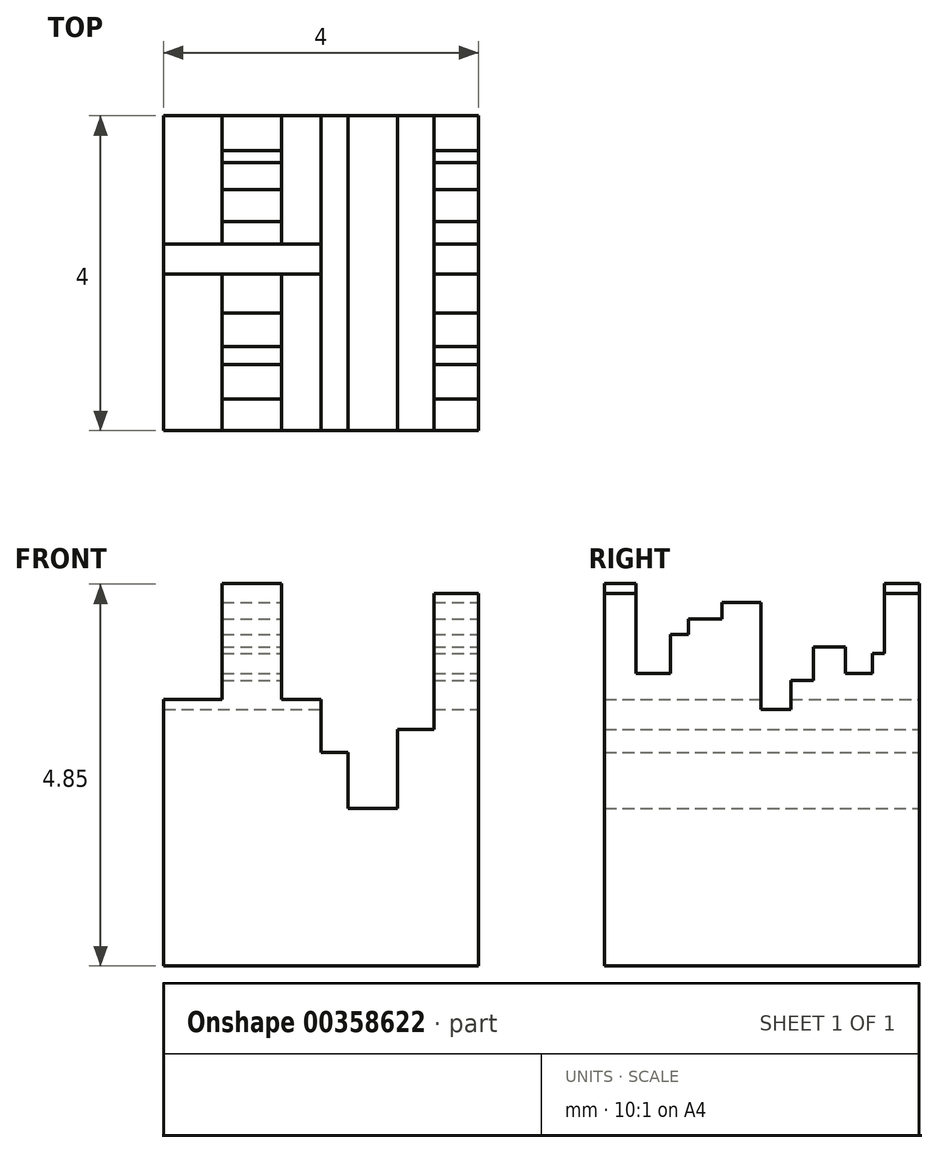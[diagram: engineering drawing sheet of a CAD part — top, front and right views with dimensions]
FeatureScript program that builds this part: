
annotation { "Feature Type Name" : "Feature", "Feature Type Description" : "" }
export const myFeature = defineFeature(function(context is Context, id is Id, definition is map)
    precondition{}
    {
        {
            var Q0;
            Q0=qCreatedBy(makeId("Front.planeOp"),FACE);
            var sketch = newSketch(context, id + "F0", { "sketchPlane" : qUnion([Q0])});
            skLineSegment(sketch, "E0.top", {"start": v(-2, -2) * mm, "end": v(2, -2) * mm});
            skLineSegment(sketch, "E0.left", {"start": v(-2, 1.38) * mm, "end": v(-2, -2) * mm});
            skLineSegment(sketch, "E0.right", {"start": v(2, 2) * mm, "end": v(2, -2) * mm});
            skPoint(sketch, "E0.middle", {"position": v(0, 0) * mm});
            skLineSegment(sketch, "E1", {"start": v(0.97, 1) * mm, "end": v(0.97, 0) * mm});
            skLineSegment(sketch, "E2", {"start": v(0.97, 0) * mm, "end": v(0.34, 0) * mm});
            skLineSegment(sketch, "E3", {"start": v(0.34, 0) * mm, "end": v(0.34, 0.71) * mm});
            skLineSegment(sketch, "E4", {"start": v(0.34, 0.71) * mm, "end": v(0, 0.71) * mm});
            skLineSegment(sketch, "E5", {"start": v(0, 0.71) * mm, "end": v(0, 1.38) * mm});
            skLineSegment(sketch, "E6", {"start": v(0, 1.38) * mm, "end": v(-0.5, 1.38) * mm});
            skLineSegment(sketch, "E7", {"start": v(-0.5, 1.38) * mm, "end": v(-0.5, 2) * mm});
            skLineSegment(sketch, "E8", {"start": v(-0.5, 2) * mm, "end": v(-0.5, 2.85) * mm});
            skLineSegment(sketch, "E9", {"start": v(-0.5, 2.85) * mm, "end": v(-1.26, 2.85) * mm});
            skLineSegment(sketch, "E10", {"start": v(-1.26, 2.85) * mm, "end": v(-1.26, 2) * mm});
            skLineSegment(sketch, "E11", {"start": v(-1.26, 2) * mm, "end": v(-1.26, 1.38) * mm});
            skLineSegment(sketch, "E12", {"start": v(-1.26, 1.38) * mm, "end": v(-2, 1.38) * mm});
            skLineSegment(sketch, "E13", {"start": v(0.97, 1) * mm, "end": v(1.43, 1) * mm});
            skLineSegment(sketch, "E14", {"start": v(1.43, 1) * mm, "end": v(1.43, 2.73) * mm});
            skLineSegment(sketch, "E15", {"start": v(1.43, 2.73) * mm, "end": v(1.94, 2.73) * mm});
            skPoint(sketch, "E16.start.orphan", {"position": v(0.97, 2) * mm});
            skPoint(sketch, "E17.orphan", {"position": v(-2, 2) * mm});
            skLineSegment(sketch, "E18", {"start": v(2, 2) * mm, "end": v(2, 2.73) * mm});
            skLineSegment(sketch, "E19", {"start": v(2, 2.73) * mm, "end": v(1.94, 2.73) * mm});
            skSolve(sketch);
        }
        {
            var Q0;
            Q0 = qSketchRegion(id + "F0", true);
            extrude(context, id + "F1", {"entities" : qUnion([Q0]), "depth" : 4 * mm});
        }
        {
            var Q0;
            Q0=makeQuery(id+"F1.opExtrude","SWEPT_FACE",FACE,{"disambiguationData":[OSD([sQuery(id+"F0.wireOp",EDGE,"E0.right"),sQuery(id+"F0.wireOp",EDGE,"E18")])]});
            var sketch = newSketch(context, id + "F2", { "sketchPlane" : qUnion([Q0])});
            skLineSegment(sketch, "E20", {"start": v(-3.6, 2.73) * mm, "end": v(-3.6, 1.71) * mm});
            skLineSegment(sketch, "E21", {"start": v(-3.6, 1.71) * mm, "end": v(-3.16, 1.71) * mm});
            skLineSegment(sketch, "E22", {"start": v(-3.16, 1.71) * mm, "end": v(-3.16, 2.21) * mm});
            skLineSegment(sketch, "E23", {"start": v(-3.16, 2.21) * mm, "end": v(-2.93, 2.21) * mm});
            skLineSegment(sketch, "E24", {"start": v(-2.93, 2.21) * mm, "end": v(-2.93, 2.4) * mm});
            skLineSegment(sketch, "E25", {"start": v(-2.93, 2.4) * mm, "end": v(-2.5, 2.4) * mm});
            skLineSegment(sketch, "E26", {"start": v(-2.5, 2.4) * mm, "end": v(-2.5, 2.61) * mm});
            skLineSegment(sketch, "E27", {"start": v(-2.5, 2.61) * mm, "end": v(-2.01, 2.61) * mm});
            skLineSegment(sketch, "E28", {"start": v(-2.01, 2.61) * mm, "end": v(-2.01, 1.25) * mm});
            skLineSegment(sketch, "E29", {"start": v(-2.01, 1.25) * mm, "end": v(-1.63, 1.25) * mm});
            skLineSegment(sketch, "E30", {"start": v(-1.63, 1.25) * mm, "end": v(-1.63, 1.62) * mm});
            skLineSegment(sketch, "E31", {"start": v(-1.63, 1.62) * mm, "end": v(-1.34, 1.62) * mm});
            skLineSegment(sketch, "E32", {"start": v(-1.34, 1.62) * mm, "end": v(-1.34, 2.05) * mm});
            skLineSegment(sketch, "E33", {"start": v(-1.34, 2.05) * mm, "end": v(-0.94, 2.05) * mm});
            skLineSegment(sketch, "E34", {"start": v(-0.94, 2.05) * mm, "end": v(-0.94, 1.71) * mm});
            skLineSegment(sketch, "E35", {"start": v(-0.94, 1.71) * mm, "end": v(-0.6, 1.71) * mm});
            skLineSegment(sketch, "E36", {"start": v(-0.6, 1.71) * mm, "end": v(-0.6, 1.97) * mm});
            skLineSegment(sketch, "E37", {"start": v(-0.6, 1.97) * mm, "end": v(-0.45, 1.97) * mm});
            skLineSegment(sketch, "E38", {"start": v(-0.45, 1.97) * mm, "end": v(-0.45, 2.73) * mm});
            skLineSegment(sketch, "E39", {"start": v(-0.45, 2.73) * mm, "end": v(0, 2.73) * mm});
            skLineSegment(sketch, "E40", {"start": v(-3.6, 2.73) * mm, "end": v(-3.6, 2.86) * mm});
            skLineSegment(sketch, "E41", {"start": v(-3.6, 2.86) * mm, "end": v(-0.7, 2.86) * mm});
            skLineSegment(sketch, "E42", {"start": v(-0.7, 2.86) * mm, "end": v(-0.45, 2.86) * mm});
            skLineSegment(sketch, "E43", {"start": v(-0.45, 2.86) * mm, "end": v(-0.45, 2.73) * mm});
            skSolve(sketch);
        }
        {
            var Q0;
            Q0 = qSketchRegion(id + "F2", true);
            extrude(context, id + "F3", {"entities" : qUnion([Q0]), "operationType" : NewBodyOperationType.REMOVE, "oppositeDirection" : true, "depth" : 25 * mm});
        }
    });
